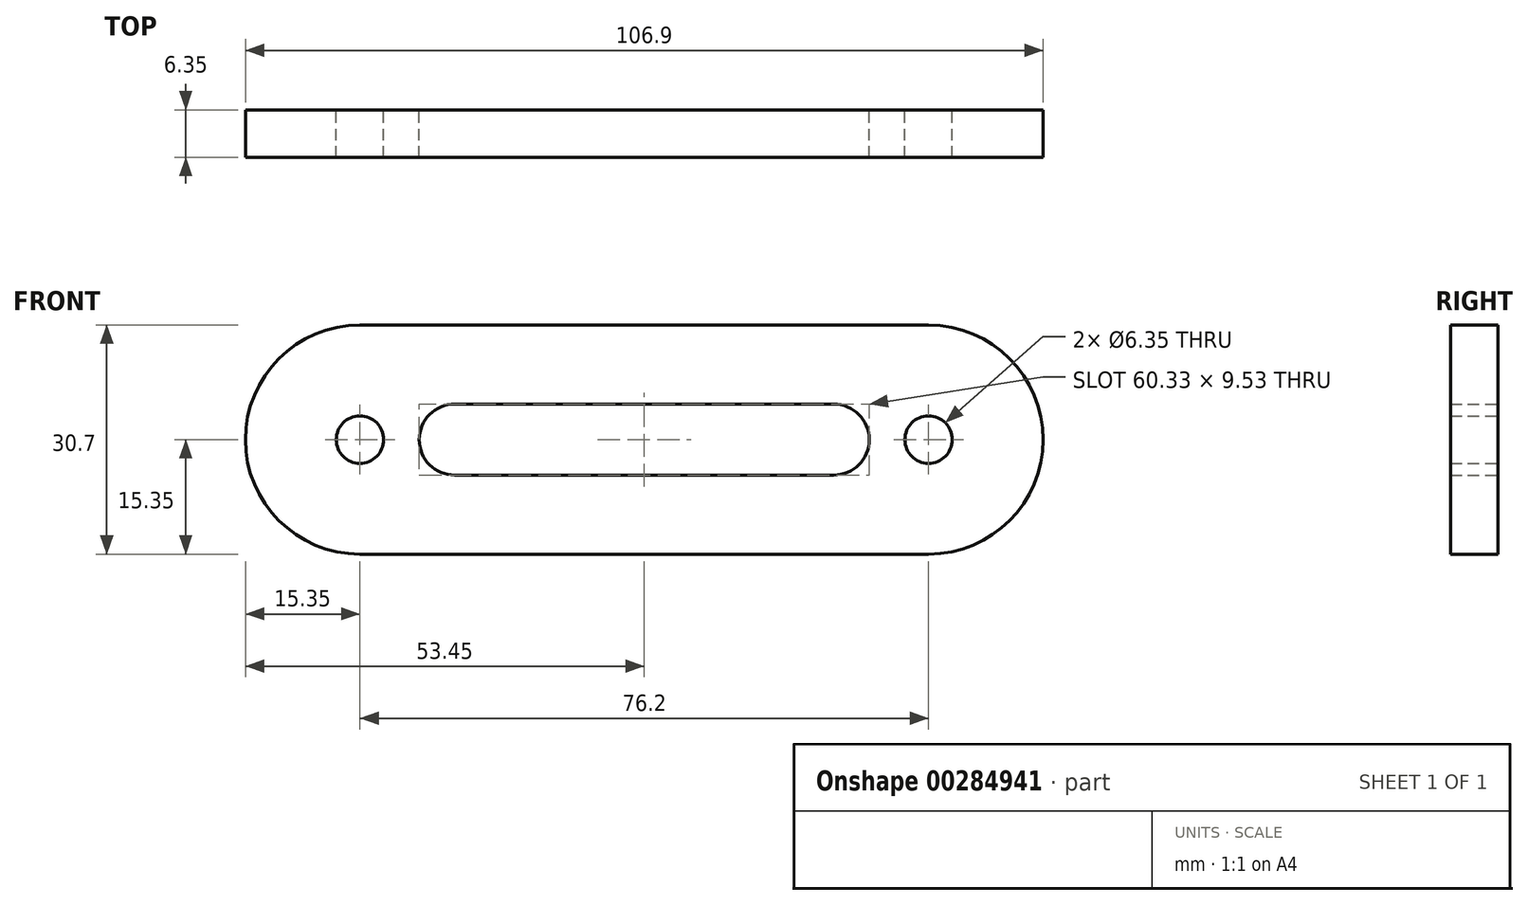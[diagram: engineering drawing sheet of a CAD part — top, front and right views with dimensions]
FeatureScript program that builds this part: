
annotation { "Feature Type Name" : "Feature", "Feature Type Description" : "" }
export const myFeature = defineFeature(function(context is Context, id is Id, definition is map)
    precondition{}
    {
        {
            var Q0;
            Q0=qCreatedBy(makeId("Front.planeOp"),FACE);
            var sketch = newSketch(context, id + "F0", { "sketchPlane" : qUnion([Q0])});
            skLineSegment(sketch, "E0.bottom", {"start": v(38.1, 15.35) * mm, "end": v(-38.1, 15.35) * mm});
            skLineSegment(sketch, "E0.top", {"start": v(38.1, -15.35) * mm, "end": v(-38.1, -15.35) * mm});
            skPoint(sketch, "E0.middle", {"position": v(0, 0) * mm});
            skArc(sketch, "E1", {"start": v(-38.1, 15.35) * mm, "mid": v(-53.45, 0) * mm, "end": v(-38.1, -15.35) * mm});
            skArc(sketch, "E2", {"start": v(38.1, -15.35) * mm, "mid": v(53.45, 0) * mm, "end": v(38.1, 15.35) * mm});
            skLineSegment(sketch, "E3.bottom", {"start": v(25.4, 4.76) * mm, "end": v(-25.4, 4.76) * mm});
            skLineSegment(sketch, "E3.top", {"start": v(25.4, -4.76) * mm, "end": v(-25.4, -4.76) * mm});
            skCircle(sketch, "E4", {"center": v(-38.1, 0) * mm, "radius": 3.18 * mm});
            skCircle(sketch, "E5", {"center": v(38.1, 0) * mm, "radius": 3.18 * mm});
            skArc(sketch, "E6", {"start": v(-25.4, 4.76) * mm, "mid": v(-30.16, 0) * mm, "end": v(-25.4, -4.76) * mm});
            skArc(sketch, "E7", {"start": v(25.4, -4.76) * mm, "mid": v(30.16, 0) * mm, "end": v(25.4, 4.76) * mm});
            skSolve(sketch);
        }
        {
            var Q0;
            Q0 = qSketchRegion(id + "F0", true);
            var Q1;
            Q1=makeQuery(id+"F0.imprint","IMPRINT",FACE,{"disambiguationData":[TD([[makeQuery(id+"F0.imprint","IMPRINT",EDGE,{"derivedFrom":sQuery(id+"F0.wireOp",EDGE,"E0.bottom")}),1.0]])]});
            extrude(context, id + "F1", {"entities" : qUnion([Q0, Q1]), "depth" : 6.35 * mm});
        }
    });
